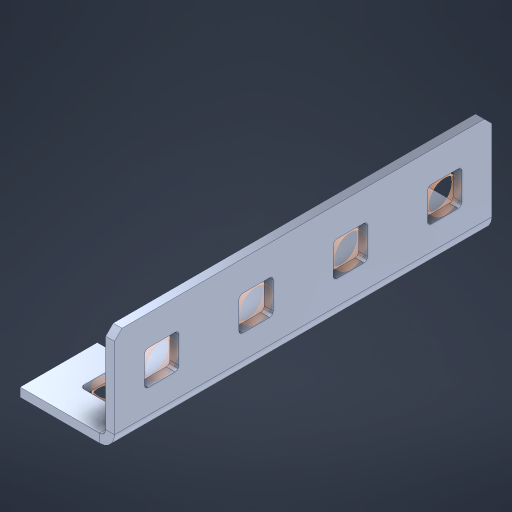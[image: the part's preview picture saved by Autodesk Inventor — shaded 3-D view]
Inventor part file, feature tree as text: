
AUTODESK INVENTOR PART (.ipt)
format: ipt  version: 2023 (Build 270158000, 158)  size: 527,872 bytes
history: native  units: in
note: dims shown in document units (in); Inventor stores cm internally (conversion verified against a paired STEP export)
features: other x19, sheet_metal_op x11, extrude x10, sketch x10, pattern_linear x2, mirror x1, chamfer x1
ambient origin geometry x8: Origin, YZ Plane, XZ Plane, XY Plane, X Axis, Y Axis, Z Axis, Center Point
bodies: Solid1 (feature_tree), Body (feature_tree)
feature tree (54):
  sheet_metal_op  "Flanges"
  other  "Flange Pattern Plane"
  other  "Flange Pattern Sketch"
  sheet_metal_op  "Flange Pattern"
  sheet_metal_op  "Body Pattern"
  pattern_linear  "Center Pattern"  Spacing1=0.0469in  [1 undecoded]
  other  "Arc Length"
  mirror  "Notch Mirror"
  pattern_linear  "Notch Pattern"  Spacing1=0.182in  [1 undecoded]
  chamfer  "End Chamfer"
  extrude  "Half Cut"  Depth=0.02in
  sketch  "Sketch1"  dims[d0=1.0in]
  other  "Plate1"
  sketch  "Sketch2"  dims[d1=2.0in]
  other  "Plate2"
  sheet_metal_op  "Bend1"
  sheet_metal_op  "Corner1"
  sketch  "Sketch3"  dims[d2=0.0469in]
  sketch  "Sketch7"  dims[d3=0.0469in]
  other  "Srf1"
  other  "Srf2"
  sketch  "Sketch8"  dims[d4=0.0234in]
  sketch  "Sketch9"  dims[d5=0.0938in]
  other  "Srf91"
  sheet_metal_op  "Body Pattern Sketch"
  other  "Srf92"
  sketch  "Sketch13"  dims[d6=0.0469in]
  sketch  "Sketch14"  dims[d7=0.5in d8=90.0deg d9=0.0312in]
  sketch  "Sketch15"  dims[d10=0.1875in]
  sketch  "Sketch16"  dims[d11=0.0469in d12=0.0469in d16=0.182in d17=0.02in d18=0.0469in d19=0.0in d20=0.25in d21=0.25in d38=1.5748in d40=0.5in d41=0.3937in d43=1.0in d46=0.172in d47=1.0in d48=0.0in d49=0.182in d50=0.02in d51=0.25in d52=0.25in d53=0.0469in d54=0.0in d55=0.172in d56=1.0in d57=0.0in d58=0.25in d60=1.5748in d62=0.5in d63=0.3937in d65=0.5in d85=0.1227in d86=0.1659in d88=0.04in d89=0.0469in d90=0.0in d91=0.04in d92=0.0491in d95=2.5in d96=0.04in d97=0.25in d98=45.0deg d99=0.25in d100=0.5in d101=0.0in d102=2.497in d106=0.182in d107=0.02in d108=0.5in d109=0.5in d110=0.0469in d111=0.0in d112=0.172in d113=0.5in d114=0.0in d117=0.5in d118=0.5in d119=0.5in]
  other  "Srf786"
  other  "Srf823"
  other  "Srf824"
  other  "Srf856"
  other  "Srf857"
  other  "Srf889"
  other  "Srf890"
  other  "Srf891"
  sheet_metal_op  "Flange Stamp"
  sheet_metal_op  "Flange Circle"
  sheet_metal_op  "Body Stamp"
  sheet_metal_op  "Body Circle"
  other  "Center Stamp"
  other  "Center Circle"
  sheet_metal_op  "Notch"
  extrude  "ExtrusionSrf2"  Depth=0.0469in
  extrude  "ExtrusionSrf92"  TaperAngle=0.0deg  [1 undecoded]
  extrude  "ExtrusionSrf823"  Depth=0.25in
  extrude  "ExtrusionSrf824"  Depth=0.25in
  extrude  "ExtrusionSrf856"  Depth=0.5in
  extrude  "ExtrusionSrf857"  Depth=0.5in
  extrude  "ExtrusionSrf889"  Depth=1.0in TaperAngle=0.0deg
  extrude  "ExtrusionSrf890"  Depth=0.182in
  extrude  "ExtrusionSrf891"  Depth=0.02in
note: 3 required parameter values undecoded (feature->parameter linkage not recoverable at this tier; creation-order binding heuristic only, values carry confidence <= 0.55)
